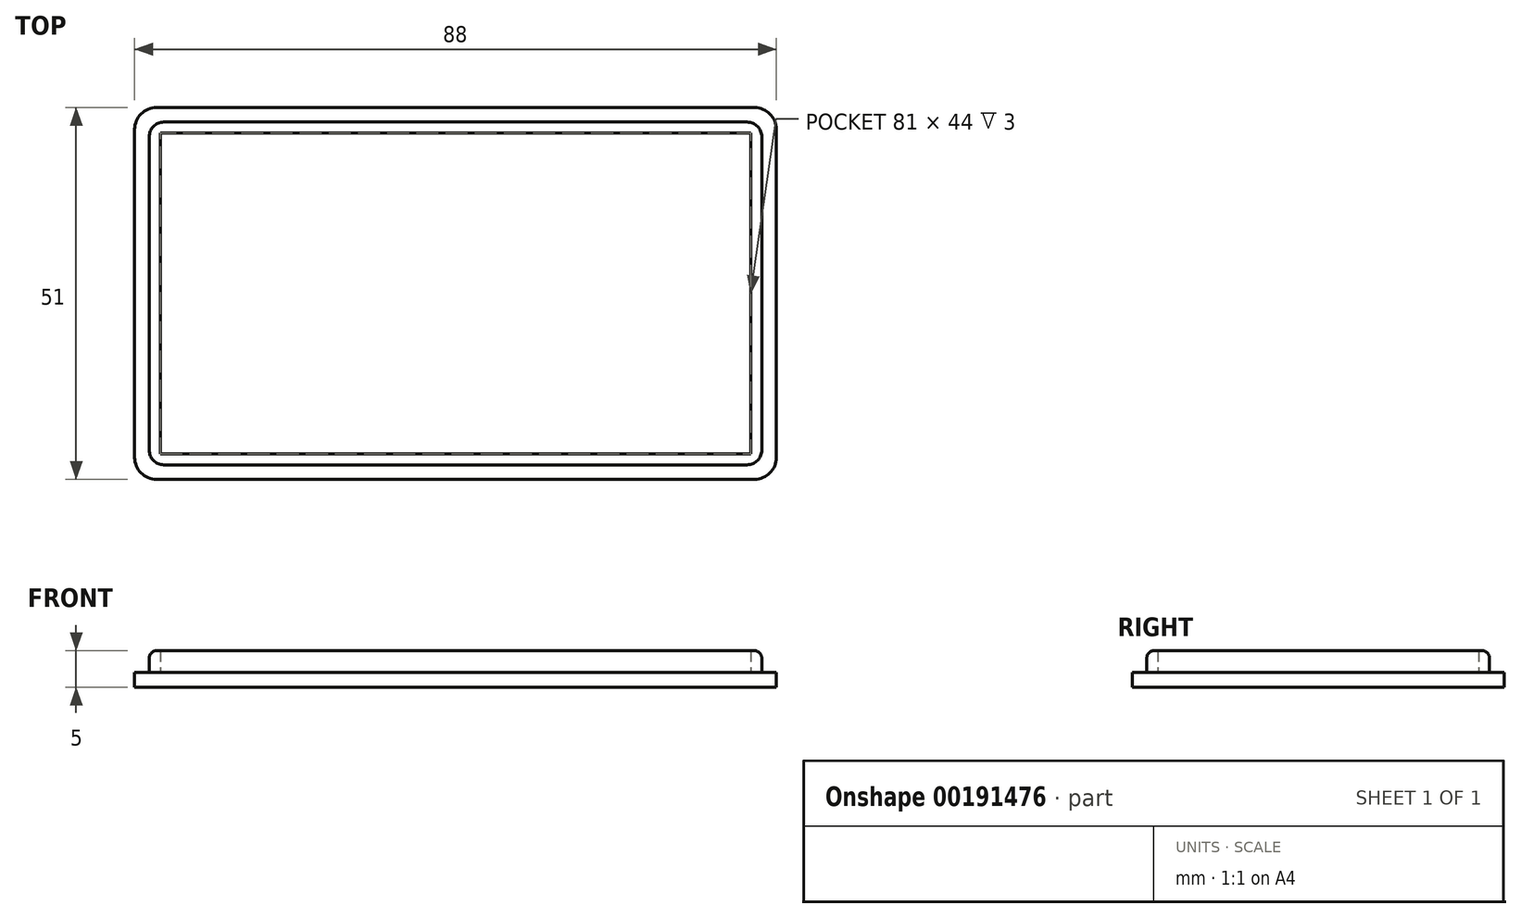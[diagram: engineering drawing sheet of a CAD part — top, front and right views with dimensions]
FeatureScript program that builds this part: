
annotation { "Feature Type Name" : "Feature", "Feature Type Description" : "" }
export const myFeature = defineFeature(function(context is Context, id is Id, definition is map)
    precondition{}
    {
        {
            var Q0;
            Q0=qCreatedBy(makeId("Top.planeOp"),FACE);
            var sketch = newSketch(context, id + "F0", { "sketchPlane" : qUnion([Q0])});
            skLineSegment(sketch, "E0.bottom", {"start": v(41, -25.5) * mm, "end": v(-41, -25.5) * mm});
            skLineSegment(sketch, "E0.top", {"start": v(41, 25.5) * mm, "end": v(-41, 25.5) * mm});
            skLineSegment(sketch, "E0.left", {"start": v(44, -22.5) * mm, "end": v(44, 22.5) * mm});
            skLineSegment(sketch, "E0.right", {"start": v(-44, -22.5) * mm, "end": v(-44, 22.5) * mm});
            skPoint(sketch, "E0.middle", {"position": v(0, 0) * mm});
            skPoint(sketch, "E1.visualSharp", {"position": v(-44, 25.5) * mm});
            skArc(sketch, "E1.filletArc", {"start": v(-41, 25.5) * mm, "mid": v(-43.12, 24.62) * mm, "end": v(-44, 22.5) * mm});
            skPoint(sketch, "E2.visualSharp", {"position": v(-44, -25.5) * mm});
            skArc(sketch, "E2.filletArc", {"start": v(-44, -22.5) * mm, "mid": v(-43.12, -24.62) * mm, "end": v(-41, -25.5) * mm});
            skPoint(sketch, "E3.visualSharp", {"position": v(44, -25.5) * mm});
            skArc(sketch, "E3.filletArc", {"start": v(41, -25.5) * mm, "mid": v(43.12, -24.62) * mm, "end": v(44, -22.5) * mm});
            skPoint(sketch, "E4.visualSharp", {"position": v(44, 25.5) * mm});
            skArc(sketch, "E4.filletArc", {"start": v(44, 22.5) * mm, "mid": v(43.12, 24.62) * mm, "end": v(41, 25.5) * mm});
            skLineSegment(sketch, "E5.0", {"start": v(40, 23.5) * mm, "end": v(-40, 23.5) * mm});
            skLineSegment(sketch, "E5.1", {"start": v(42, -21.5) * mm, "end": v(42, 21.5) * mm});
            skLineSegment(sketch, "E5.2", {"start": v(40, -23.5) * mm, "end": v(-40, -23.5) * mm});
            skLineSegment(sketch, "E5.3", {"start": v(-42, -21.5) * mm, "end": v(-42, 21.5) * mm});
            skPoint(sketch, "E6.visualSharp", {"position": v(-42, 23.5) * mm});
            skArc(sketch, "E6.filletArc", {"start": v(-40, 23.5) * mm, "mid": v(-41.41, 22.91) * mm, "end": v(-42, 21.5) * mm});
            skPoint(sketch, "E7.visualSharp", {"position": v(42, 23.5) * mm});
            skArc(sketch, "E7.filletArc", {"start": v(42, 21.5) * mm, "mid": v(41.41, 22.91) * mm, "end": v(40, 23.5) * mm});
            skPoint(sketch, "E8.visualSharp", {"position": v(42, -23.5) * mm});
            skArc(sketch, "E8.filletArc", {"start": v(40, -23.5) * mm, "mid": v(41.41, -22.91) * mm, "end": v(42, -21.5) * mm});
            skPoint(sketch, "E9.visualSharp", {"position": v(-42, -23.5) * mm});
            skArc(sketch, "E9.filletArc", {"start": v(-42, -21.5) * mm, "mid": v(-41.41, -22.91) * mm, "end": v(-40, -23.5) * mm});
            skLineSegment(sketch, "E10.0", {"start": v(40.5, 22) * mm, "end": v(-40.5, 22) * mm});
            skLineSegment(sketch, "E10.1", {"start": v(40.5, -22) * mm, "end": v(40.5, 22) * mm});
            skLineSegment(sketch, "E10.2", {"start": v(40.5, -22) * mm, "end": v(-40.5, -22) * mm});
            skLineSegment(sketch, "E10.3", {"start": v(-40.5, -22) * mm, "end": v(-40.5, 22) * mm});
            skSolve(sketch);
        }
        {
            var Q0;
            Q0 = qSketchRegion(id + "F0", true);
            var Q1;
            Q1=makeQuery(id+"F0.imprint","IMPRINT",FACE,{"disambiguationData":[TD([[makeQuery(id+"F0.imprint","IMPRINT",EDGE,{"derivedFrom":sQuery(id+"F0.wireOp",EDGE,"E10.0")}),1.0]])]});
            var Q2;
            Q2=makeQuery(id+"F0.imprint","IMPRINT",FACE,{"disambiguationData":[TD([[makeQuery(id+"F0.imprint","IMPRINT",EDGE,{"derivedFrom":sQuery(id+"F0.wireOp",EDGE,"E5.0")}),1.0]])]});
            extrude(context, id + "F1", {"entities" : qUnion([Q0, Q1, Q2]), "depth" : 2 * mm});
        }
        {
            var Q0;
            Q0=makeQuery(id+"F0.imprint","IMPRINT",FACE,{"disambiguationData":[TD([[makeQuery(id+"F0.imprint","IMPRINT",EDGE,{"derivedFrom":sQuery(id+"F0.wireOp",EDGE,"E5.0")}),1.0]])]});
            extrude(context, id + "F2", {"entities" : qUnion([Q0]), "operationType" : NewBodyOperationType.ADD, "depth" : 5 * mm});
        }
        {
            var Q0;
            Q0=makeQuery(id+"F2.opExtrude","CAP_EDGE",EDGE,{"disambiguationData":[OSD([sQuery(id+"F0.wireOp",EDGE,"E5.3")])],"isStart":false});
            fillet(context, id + "F3", {"entities" : qUnion([Q0]), "radius" : 1 * mm, "tangentPropagation" : true, "allowEdgeOverflow" : false});
        }
    });
